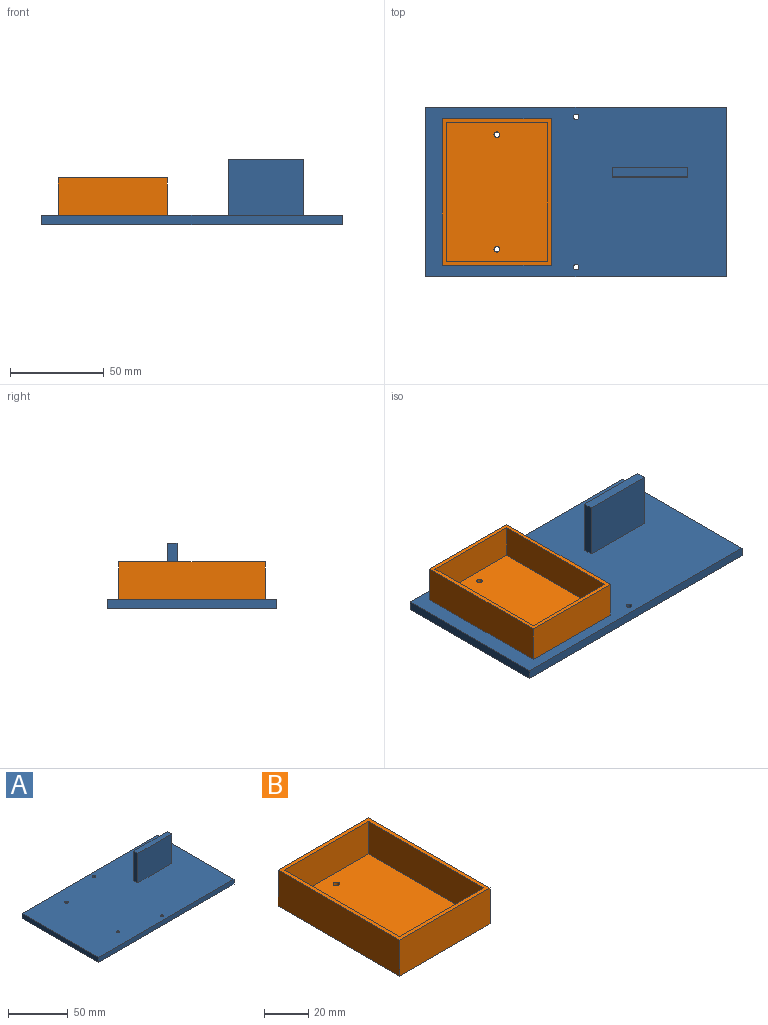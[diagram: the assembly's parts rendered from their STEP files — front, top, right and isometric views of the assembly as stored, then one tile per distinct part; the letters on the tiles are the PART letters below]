
ASSEMBLY  parts=2 mates=1
PART A: 15 faces, bbox 160x90x35 mm
  f0: plane 160x90mm, normal (0,0,1), area 14171.7mm2, adj f1,f2,f3,f4,f6,f7,f8,f9
  f1: plane 160x5mm, normal (0,1,0), area 800mm2, adj f0,f2,f4,f5
  f2: plane 90x5mm, normal (-1,0,0), area 450mm2, adj f0,f1,f3,f5
  f3: plane 160x5mm, normal (0,-1,0), area 800mm2, adj f0,f2,f4,f5
  f4: plane 90x5mm, normal (1,0,0), area 450mm2, adj f0,f1,f3,f5
  f5: plane 160x90mm, normal (0,0,-1), area 14371.7mm2, adj f1,f2,f3,f4,f6,f7,f8,f9
  f6: cylinder r=1.5mm len=5mm, axis (0,0,1), area 47.1mm2, adj f0,f5
  f7: cylinder r=1.5mm len=5mm, axis (0,0,1), area 47.1mm2, adj f0,f5
  f8: cylinder r=1.5mm len=5mm, axis (0,0,1), area 47.1mm2, adj f0,f5
  f9: cylinder r=1.5mm len=5mm, axis (0,0,1), area 47.1mm2, adj f0,f5
  f10: plane 40x30mm, normal (0,1,0), area 1200mm2, adj f0,f11,f13,f14
  f11: plane 30x5mm, normal (-1,0,0), area 150mm2, adj f0,f10,f12,f14
  f12: plane 40x30mm, normal (0,-1,0), area 1200mm2, adj f0,f11,f13,f14
  f13: plane 30x5mm, normal (1,0,0), area 150mm2, adj f0,f10,f12,f14
  f14: plane 40x5mm, normal (0,0,1), area 200mm2, adj f10,f11,f12,f13
PART B: 13 faces, bbox 58x78x20 mm
  f0: cylinder r=1.5mm len=3mm, axis (0,0,-1), area 18.8mm2, adj f7,f12
  f1: cylinder r=1.5mm len=3mm, axis (0,0,-1), area 18.8mm2, adj f7,f12
  f2: plane 78x58mm, normal (0,0,1), area 528mm2, adj f3,f4,f5,f6,f8,f9,f10,f11
  f3: plane 58x20mm, normal (0,1,0), area 1160mm2, adj f2,f4,f6,f7
  f4: plane 78x20mm, normal (-1,0,0), area 1560mm2, adj f2,f3,f5,f7
  f5: plane 58x20mm, normal (0,-1,0), area 1160mm2, adj f2,f4,f6,f7
  f6: plane 78x20mm, normal (1,0,0), area 1560mm2, adj f2,f3,f5,f7
  f7: plane 78x58mm, normal (0,0,-1), area 4509.9mm2, adj f0,f1,f3,f4,f5,f6
  f8: plane 54x18mm, normal (0,-1,0), area 972mm2, adj f2,f9,f11,f12
  f9: plane 74x18mm, normal (1,0,0), area 1332mm2, adj f2,f8,f10,f12
  f10: plane 54x18mm, normal (0,1,0), area 972mm2, adj f2,f9,f11,f12
  f11: plane 74x18mm, normal (-1,0,0), area 1332mm2, adj f2,f8,f10,f12
  f12: plane 74x54mm, normal (0,0,1), area 3981.9mm2, adj f0,f1,f8,f9,f10,f11
PLACE A t=(4.2,-0.48,-6.86)mm
PLACE B t=(-37.99,-0.48,-1.86)mm
MATE fastened B.f0 <-> A.f7  axis (0,0,-1) through (-37.99,30.02,-1.86)mm
